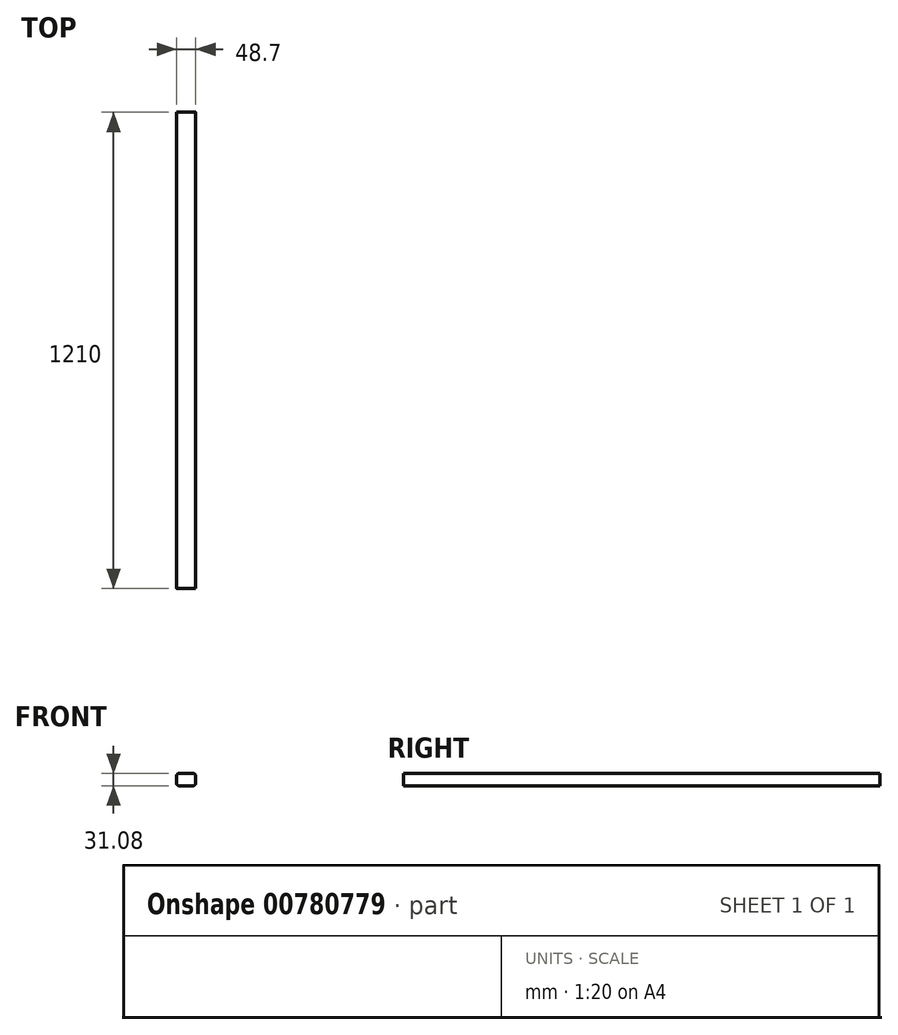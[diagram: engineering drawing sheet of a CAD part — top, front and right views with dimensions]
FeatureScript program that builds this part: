
annotation { "Feature Type Name" : "Feature", "Feature Type Description" : "" }
export const myFeature = defineFeature(function(context is Context, id is Id, definition is map)
    precondition{}
    {
        {
            var Q0;
            Q0=qCreatedBy(makeId("Front.planeOp"),FACE);
            var sketch = newSketch(context, id + "F0", { "sketchPlane" : qUnion([Q0])});
            skLineSegment(sketch, "E0.bottom", {"start": v(18, -15.54) * mm, "end": v(-18, -15.54) * mm});
            skLineSegment(sketch, "E0.top", {"start": v(18, 15.54) * mm, "end": v(-18, 15.54) * mm});
            skLineSegment(sketch, "E0.left", {"start": v(24.35, -9.19) * mm, "end": v(24.35, 9.19) * mm});
            skLineSegment(sketch, "E0.right", {"start": v(-24.35, -9.19) * mm, "end": v(-24.35, 9.19) * mm});
            skPoint(sketch, "E0.middle", {"position": v(0, 0) * mm});
            skPoint(sketch, "E1.visualSharp", {"position": v(-24.35, 15.54) * mm});
            skArc(sketch, "E1.filletArc", {"start": v(-18, 15.54) * mm, "mid": v(-22.49, 13.68) * mm, "end": v(-24.35, 9.19) * mm});
            skPoint(sketch, "E2.visualSharp", {"position": v(24.35, -15.54) * mm});
            skArc(sketch, "E2.filletArc", {"start": v(18, -15.54) * mm, "mid": v(22.49, -13.68) * mm, "end": v(24.35, -9.19) * mm});
            skPoint(sketch, "E3.visualSharp", {"position": v(24.35, 15.54) * mm});
            skArc(sketch, "E3.filletArc", {"start": v(24.35, 9.19) * mm, "mid": v(22.49, 13.68) * mm, "end": v(18, 15.54) * mm});
            skPoint(sketch, "E4.visualSharp", {"position": v(-24.35, -15.54) * mm});
            skArc(sketch, "E4.filletArc", {"start": v(-24.35, -9.19) * mm, "mid": v(-22.49, -13.68) * mm, "end": v(-18, -15.54) * mm});
            skSolve(sketch);
        }
        {
            var Q0;
            Q0=makeQuery(id+"F0.imprint","IMPRINT",FACE,{"disambiguationData":[TD([[makeQuery(id+"F0.imprint","IMPRINT",EDGE,{"derivedFrom":sQuery(id+"F0.wireOp",EDGE,"E0.bottom")}),-1.0]])]});
            extrude(context, id + "F1", {"entities" : qUnion([Q0]), "depth" : 1210 * mm, "offsetDistance" : 25.4 * mm});
        }
    });
